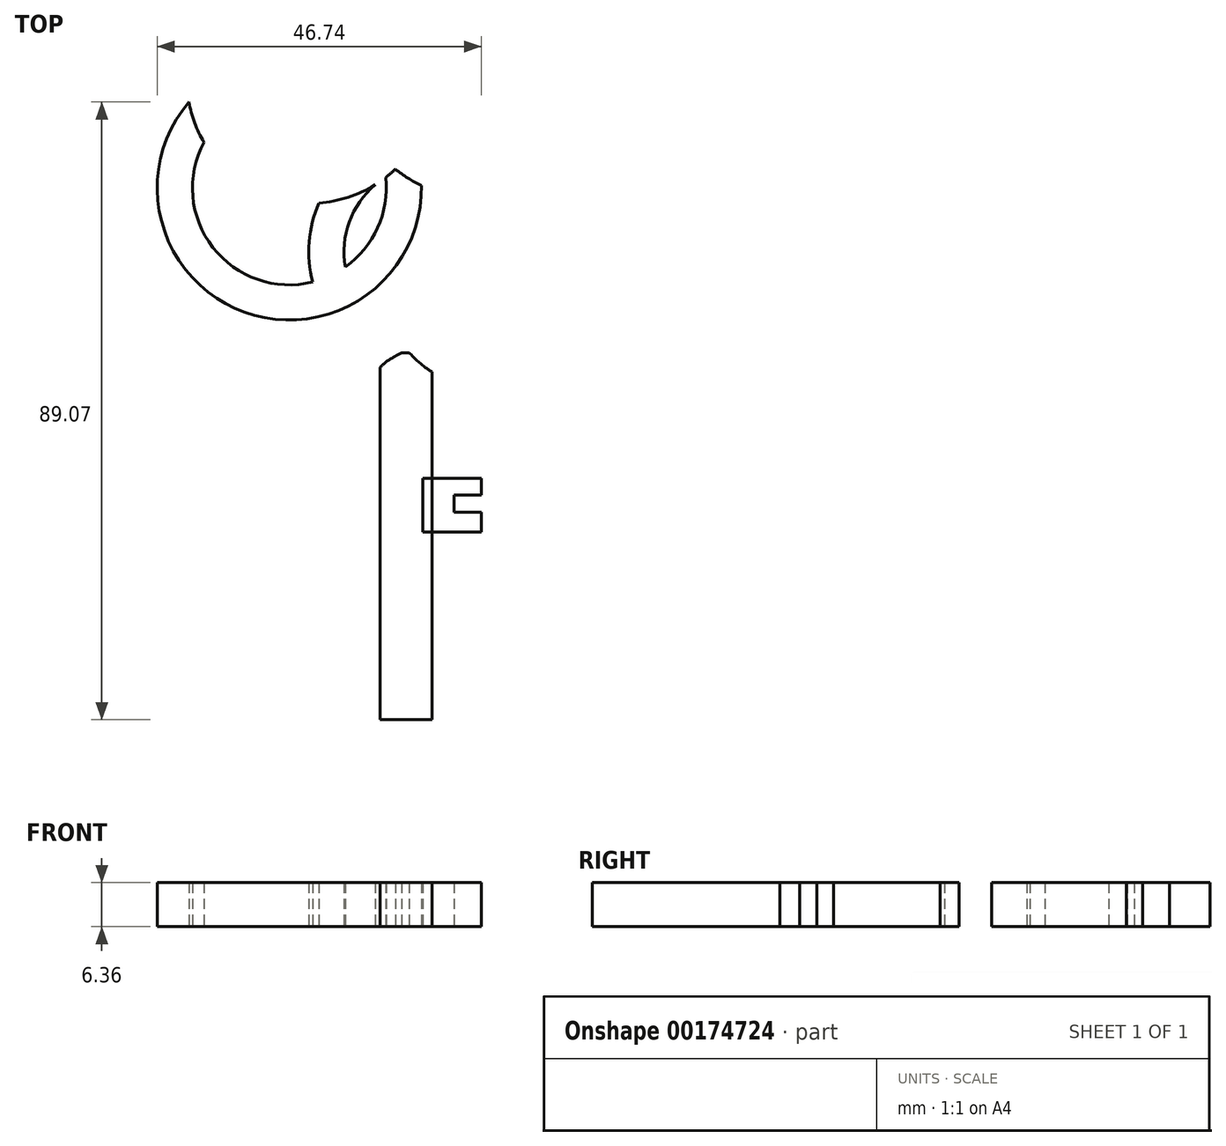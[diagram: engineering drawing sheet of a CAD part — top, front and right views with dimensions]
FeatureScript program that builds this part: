
annotation { "Feature Type Name" : "Feature", "Feature Type Description" : "" }
export const myFeature = defineFeature(function(context is Context, id is Id, definition is map)
    precondition{}
    {
        {
            var Q0;
            Q0=qCreatedBy(makeId("Top.planeOp"),FACE);
            var sketch = newSketch(context, id + "F0", { "sketchPlane" : qUnion([Q0])});
            skArc(sketch, "E0", {"start": v(-10.33, 40.05) * mm, "mid": v(-10.45, 35.3) * mm, "end": v(-8.49, 30.97) * mm});
            skArc(sketch, "E1", {"start": v(-7.9, 44.57) * mm, "mid": v(-25.63, 41.67) * mm, "end": v(-31.78, 24.8) * mm});
            skArc(sketch, "E2", {"start": v(-1.66, 43.02) * mm, "mid": v(16.48, 12.72) * mm, "end": v(5.78, 46.38) * mm});
            skArc(sketch, "E3", {"start": v(-13.04, 10.24) * mm, "mid": v(-14.44, 4.62) * mm, "end": v(-13.97, -1.16) * mm});
            skArc(sketch, "E4", {"start": v(-31.78, 24.8) * mm, "mid": v(-33.33, 2.09) * mm, "end": v(-12.02, -5.9) * mm});
            skArc(sketch, "E5", {"start": v(-5.84, 37.46) * mm, "mid": v(5.8, 36.78) * mm, "end": v(-5.71, 38.65) * mm});
            skArc(sketch, "E6", {"start": v(-10.33, 40.05) * mm, "mid": v(-21.4, 38.5) * mm, "end": v(-26.96, 28.83) * mm});
            skArc(sketch, "E7", {"start": v(-3.13, 14.13) * mm, "mid": v(-8.24, 8.52) * mm, "end": v(-9.24, 1) * mm});
            skArc(sketch, "E8", {"start": v(-29.63, 19) * mm, "mid": v(-28.34, 3.83) * mm, "end": v(-13.97, -1.16) * mm});
            skArc(sketch, "E9.trimOffspring", {"start": v(5.78, 46.38) * mm, "mid": v(-1.4, 48) * mm, "end": v(-7.9, 44.57) * mm});
            skArc(sketch, "E10.trimOffspring", {"start": v(-1.66, 43.02) * mm, "mid": v(-2.62, 42.65) * mm, "end": v(-3.5, 42.1) * mm});
            skArc(sketch, "E11.trimOffspring", {"start": v(-8.49, 30.97) * mm, "mid": v(-8.56, 30.16) * mm, "end": v(-8.6, 29.34) * mm});
            skArc(sketch, "E12.trimOffspring", {"start": v(3.48, 27.34) * mm, "mid": v(8.73, 31.3) * mm, "end": v(10.66, 37.58) * mm});
            skArc(sketch, "E13.trimOffspring", {"start": v(-29.63, 19) * mm, "mid": v(-22.58, 12.25) * mm, "end": v(-13.04, 10.24) * mm});
            skArc(sketch, "E14.trimOffspring", {"start": v(-26.08, 23.27) * mm, "mid": v(-18.42, 15.97) * mm, "end": v(-7.88, 17.02) * mm});
            skArc(sketch, "E15.trimOffspring", {"start": v(-3.13, 14.13) * mm, "mid": v(-25.3, 41.94) * mm, "end": v(-3.42, 13.9) * mm});
            skArc(sketch, "E16.trimOffspring", {"start": v(-9.24, 1) * mm, "mid": v(-4.58, 6.66) * mm, "end": v(-3.42, 13.9) * mm});
            skArc(sketch, "E17.trimOffspring", {"start": v(-7.33, -3.82) * mm, "mid": v(10.97, -6.94) * mm, "end": v(12.84, 11.53) * mm});
            skArc(sketch, "E18.trimOffspring", {"start": v(-12.02, -5.9) * mm, "mid": v(12.93, -11.76) * mm, "end": v(17.82, 13.4) * mm});
            skArc(sketch, "E19.trimOffspring", {"start": v(-7.33, -3.82) * mm, "mid": v(-0.6, 3.27) * mm, "end": v(1.73, 12.78) * mm});
            skArc(sketch, "E20.trimOffspring", {"start": v(12.97, 18.08) * mm, "mid": v(16.43, 28.37) * mm, "end": v(10.66, 37.58) * mm});
            skArc(sketch, "E21.trimOffspring", {"start": v(17.82, 13.4) * mm, "mid": v(25.87, 35.02) * mm, "end": v(5.78, 46.38) * mm});
            skArc(sketch, "E22.trimOffspring", {"start": v(9.67, 14.14) * mm, "mid": v(7.1, 15.28) * mm, "end": v(4.36, 15.82) * mm});
            skArc(sketch, "E23.trimOffspring", {"start": v(12.97, 18.08) * mm, "mid": v(7.73, 20.38) * mm, "end": v(2.02, 20.9) * mm});
            skArc(sketch, "E24.trimOffspring", {"start": v(-2.25, 32.03) * mm, "mid": v(-26.9, 26.47) * mm, "end": v(-1.64, 26.89) * mm});
            skArc(sketch, "E25.trimOffspring", {"start": v(2.94, 32.37) * mm, "mid": v(-31.97, 26.08) * mm, "end": v(3.48, 27.34) * mm});
            skArc(sketch, "E26.trimOffspring", {"start": v(1.73, 12.78) * mm, "mid": v(7.19, 11.26) * mm, "end": v(12.84, 11.53) * mm});
            skArc(sketch, "E27.trimOffspring", {"start": v(-6.23, 27.9) * mm, "mid": v(-30.54, -1.3) * mm, "end": v(-2.22, 24.02) * mm});
            skArc(sketch, "E28.trimOffspring", {"start": v(-4.96, 18.93) * mm, "mid": v(-6.47, 18.04) * mm, "end": v(-7.88, 17.02) * mm});
            skArc(sketch, "E29.trimOffspring", {"start": v(-4.96, 18.93) * mm, "mid": v(-14.5, 26.08) * mm, "end": v(-26.08, 23.27) * mm});
            skArc(sketch, "E30.trimOffspring", {"start": v(2.02, 20.9) * mm, "mid": v(3.05, 24.06) * mm, "end": v(3.48, 27.34) * mm});
            skArc(sketch, "E31.trimOffspring", {"start": v(4.36, 15.82) * mm, "mid": v(6.92, 14.69) * mm, "end": v(9.67, 14.14) * mm});
            skArc(sketch, "E32.trimOffspring", {"start": v(-8.6, 29.34) * mm, "mid": v(-17.85, 31.44) * mm, "end": v(-26.96, 28.83) * mm});
            skArc(sketch, "E33.trimOffspring", {"start": v(0.36, 19.5) * mm, "mid": v(-0.78, 21.85) * mm, "end": v(-2.22, 24.02) * mm});
            skArc(sketch, "E34", {"start": v(11.03, 46.6) * mm, "mid": v(-0.64, 51.76) * mm, "end": v(-11.8, 45.58) * mm});
            skArc(sketch, "E35.trimOffspring", {"start": v(-8.49, 30.97) * mm, "mid": v(25.9, 22.88) * mm, "end": v(-5.71, 38.65) * mm});
            skArc(sketch, "E36.trimOffspring", {"start": v(-3.1, 41.8) * mm, "mid": v(-7.2, 44.28) * mm, "end": v(-11.8, 45.58) * mm});
            skArc(sketch, "E37.trimOffspring", {"start": v(-10.33, 40.05) * mm, "mid": v(-20.62, 16.97) * mm, "end": v(-5.84, 37.46) * mm});
            skArc(sketch, "E38.trimOffspring", {"start": v(-2.22, 24.02) * mm, "mid": v(-2.02, 24.71) * mm, "end": v(-1.85, 25.42) * mm});
            skArc(sketch, "E39.trimOffspring", {"start": v(12.97, 18.08) * mm, "mid": v(23.32, 29.19) * mm, "end": v(10.66, 37.58) * mm});
            skArc(sketch, "E40.trimOffspring", {"start": v(-1.85, 25.42) * mm, "mid": v(-1.12, 22.32) * mm, "end": v(0.36, 19.5) * mm});
            skArc(sketch, "E41.trimOffspring", {"start": v(-7.9, 44.57) * mm, "mid": v(-22.97, 12.46) * mm, "end": v(-3.5, 42.1) * mm});
            skArc(sketch, "E42.trimOffspring", {"start": v(11.03, 46.6) * mm, "mid": v(3.44, 45.75) * mm, "end": v(-3.1, 41.8) * mm});
            skArc(sketch, "E43.trimOffspring", {"start": v(-8.6, 29.34) * mm, "mid": v(-36.27, 14.24) * mm, "end": v(-12.02, -5.9) * mm});
            skSolve(sketch);
        }
        {
            var Q0;
            Q0=makeQuery(id+"F0.imprint","IMPRINT",FACE,{"disambiguationData":[TD([[makeQuery(id+"F0.imprint","IMPRINT",EDGE,{"derivedFrom":sQuery(id+"F0.wireOp",EDGE,"E3")}),1.0]])]});
            extrude(context, id + "F1", {"entities" : qUnion([Q0]), "endBound" : BoundingType.SYMMETRIC, "depth" : 6.35 * mm});
        }
        {
            var Q0;
            Q0=qCreatedBy(makeId("Top.planeOp"),FACE);
            var sketch = newSketch(context, id + "F2", { "sketchPlane" : qUnion([Q0])});
            skLineSegment(sketch, "E44", {"start": v(-4.2, -13.48) * mm, "end": v(-4.2, -64.28) * mm});
            skLineSegment(sketch, "E45", {"start": v(-4.2, -64.28) * mm, "end": v(0, -64.28) * mm});
            skLineSegment(sketch, "E46", {"start": v(0, -64.28) * mm, "end": v(0, -11.35) * mm});
            skFitSpline(sketch, "E47", {"points": [v(-4.2, -13.48) * mm, v(-1.1, -11.35) * mm], "startDerivative": vector(2.3, 2.44) * mm, "endDerivative": vector(6.7, 3.66) * mm});
            skLineSegment(sketch, "E48", {"start": v(-1.1, -11.35) * mm, "end": v(0, -11.35) * mm});
            skLineSegment(sketch, "E49", {"start": v(0, -64.28) * mm, "end": v(3.25, -64.28) * mm});
            skLineSegment(sketch, "E50", {"start": v(3.25, -64.28) * mm, "end": v(3.25, -14.1) * mm});
            skFitSpline(sketch, "E51", {"points": [v(0, -11.35) * mm, v(3.25, -14.1) * mm], "startDerivative": vector(2.79, -3.35) * mm, "endDerivative": vector(2.45, -1.29) * mm});
            skSolve(sketch);
        }
        {
            var Q0;
            Q0 = qSketchRegion(id + "F2", true);
            extrude(context, id + "F3", {"entities" : qUnion([Q0]), "operationType" : NewBodyOperationType.ADD, "endBound" : BoundingType.SYMMETRIC, "depth" : 6.35 * mm});
        }
        {
            var Q0;
            Q0=qCreatedBy(makeId("Top.planeOp"),FACE);
            var sketch = newSketch(context, id + "F4", { "sketchPlane" : qUnion([Q0])});
            skLineSegment(sketch, "E52.bottom", {"start": v(2.68, -17.44) * mm, "end": v(-2.8, -17.44) * mm});
            skLineSegment(sketch, "E52.top", {"start": v(2.68, -18.75) * mm, "end": v(-2.8, -18.75) * mm});
            skLineSegment(sketch, "E52.left", {"start": v(2.68, -17.44) * mm, "end": v(2.68, -18.75) * mm});
            skLineSegment(sketch, "E52.right", {"start": v(-2.8, -17.44) * mm, "end": v(-2.8, -18.75) * mm});
            skSolve(sketch);
        }
        {
            var Q0;
            Q0 = qSketchRegion(id + "F4", true);
            extrude(context, id + "F5", {"entities" : qUnion([Q0]), "operationType" : NewBodyOperationType.ADD, "endBound" : BoundingType.SYMMETRIC, "depth" : 6.35 * mm});
        }
        {
            var Q0;
            Q0=qCreatedBy(makeId("Top.planeOp"),FACE);
            var sketch = newSketch(context, id + "F6", { "sketchPlane" : qUnion([Q0])});
            skLineSegment(sketch, "E53", {"start": v(1.92, -29.48) * mm, "end": v(10.38, -29.48) * mm});
            skLineSegment(sketch, "E54", {"start": v(10.38, -29.48) * mm, "end": v(10.38, -31.89) * mm});
            skLineSegment(sketch, "E55", {"start": v(10.38, -31.89) * mm, "end": v(6.44, -31.89) * mm});
            skLineSegment(sketch, "E56", {"start": v(6.44, -31.89) * mm, "end": v(6.44, -34.37) * mm});
            skLineSegment(sketch, "E57", {"start": v(6.44, -34.37) * mm, "end": v(10.38, -34.37) * mm});
            skLineSegment(sketch, "E58", {"start": v(10.38, -34.37) * mm, "end": v(10.38, -37.22) * mm});
            skLineSegment(sketch, "E59", {"start": v(10.38, -37.22) * mm, "end": v(1.92, -37.22) * mm});
            skLineSegment(sketch, "E60", {"start": v(1.92, -37.22) * mm, "end": v(1.92, -29.48) * mm});
            skSolve(sketch);
        }
        {
            var Q0;
            Q0 = qSketchRegion(id + "F6", true);
            extrude(context, id + "F7", {"entities" : qUnion([Q0]), "endBound" : BoundingType.SYMMETRIC, "depth" : 6.35 * mm});
        }
    });
